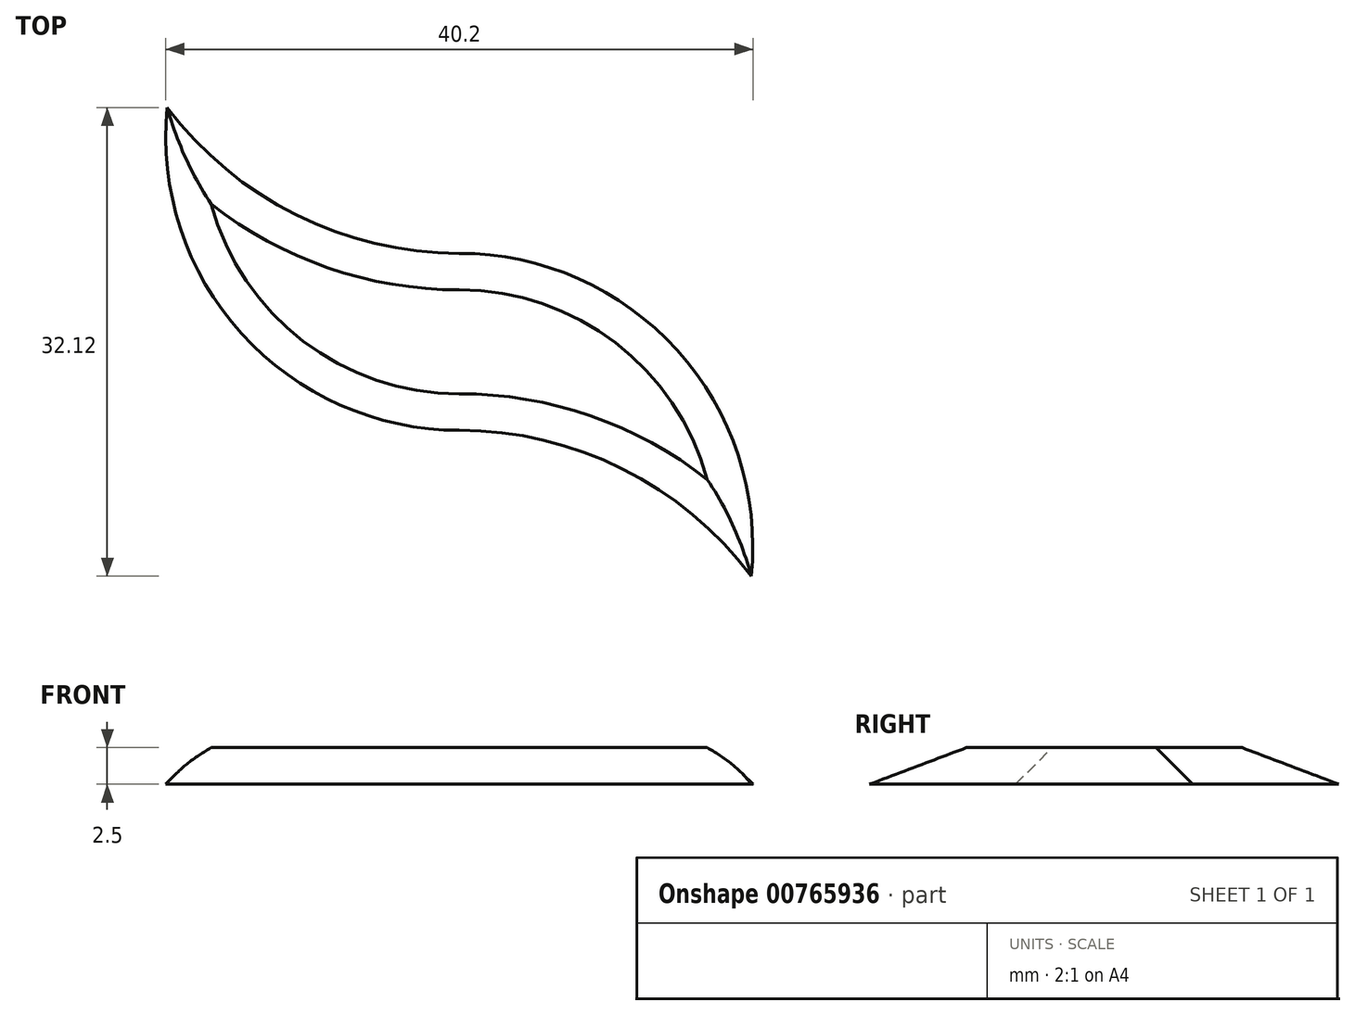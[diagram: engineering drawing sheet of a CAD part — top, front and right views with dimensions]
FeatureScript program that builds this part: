
annotation { "Feature Type Name" : "Feature", "Feature Type Description" : "" }
export const myFeature = defineFeature(function(context is Context, id is Id, definition is map)
    precondition{}
    {
        {
            var Q0;
            Q0=qCreatedBy(makeId("Top.planeOp"),FACE);
            var sketch = newSketch(context, id + "F0", { "sketchPlane" : qUnion([Q0])});
            skLineSegment(sketch, "E0.2", {"start": v(-6.06, -6.06) * mm, "end": v(-6.06, 6.06) * mm});
            skArc(sketch, "E1", {"start": v(-26.06, 16.06) * mm, "mid": v(-20.97, 0.56) * mm, "end": v(-6.06, -6.06) * mm});
            skArc(sketch, "E2", {"start": v(-26.06, 16.06) * mm, "mid": v(-17.24, 8.7) * mm, "end": v(-6.06, 6.06) * mm});
            skPoint(sketch, "E3", {"position": v(13.94, -16.06) * mm});
            skLineSegment(sketch, "E4.bottom", {"start": v(-6.06, -6.06) * mm, "end": v(6.24, -6.06) * mm, "construction": true});
            skLineSegment(sketch, "E4.left", {"start": v(-6.06, -6.06) * mm, "end": v(-6.06, 6.05) * mm, "construction": true});
            skArc(sketch, "E5", {"start": v(13.94, -16.06) * mm, "mid": v(5.12, -8.7) * mm, "end": v(-6.06, -6.06) * mm});
            skLineSegment(sketch, "E6", {"start": v(-6.06, 6.06) * mm, "end": v(10.73, 6.06) * mm, "construction": true});
            skArc(sketch, "E7", {"start": v(13.94, -16.06) * mm, "mid": v(8.85, -0.56) * mm, "end": v(-6.06, 6.06) * mm});
            skSolve(sketch);
        }
        {
            var Q0;
            Q0=makeQuery(id+"F0.imprint","IMPRINT",FACE,{"disambiguationData":[TD([[makeQuery(id+"F0.imprint","IMPRINT",EDGE,{"derivedFrom":sQuery(id+"F0.wireOp",EDGE,"E0.2")}),1.0]])]});
            var Q1;
            Q1=makeQuery(id+"F0.imprint","IMPRINT",FACE,{"disambiguationData":[TD([[makeQuery(id+"F0.imprint","IMPRINT",EDGE,{"derivedFrom":sQuery(id+"F0.wireOp",EDGE,"E0.0")}),1.0]])]});
            extrude(context, id + "F1", {"entities" : qUnion([Q0, Q1]), "depth" : 2.5 * mm, "offsetDistance" : 25 * mm});
        }
        {
            var Q0;
            Q0=makeQuery(id+"F0.imprint","IMPRINT",FACE,{"disambiguationData":[TD([[makeQuery(id+"F0.imprint","IMPRINT",EDGE,{"derivedFrom":sQuery(id+"F0.wireOp",EDGE,"E0.2")}),-1.0]])]});
            extrude(context, id + "F2", {"entities" : qUnion([Q0]), "operationType" : NewBodyOperationType.ADD, "depth" : 2.5 * mm, "offsetDistance" : 25 * mm});
        }
        {
            var Q0;
            Q0=makeQuery(id+"F1.opExtrude","CAP_EDGE",EDGE,{"disambiguationData":[OSD([sQuery(id+"F0.wireOp",EDGE,"E1")])],"isStart":false});
            var Q1;
            Q1=makeQuery(id+"F2.opExtrude","CAP_EDGE",EDGE,{"disambiguationData":[OSD([sQuery(id+"F0.wireOp",EDGE,"E7")])],"isStart":false});
            chamfer(context, id + "F3", {"entities" : qUnion([Q0, Q1]), "width" : 2.5 * mm, "tangentPropagation" : true});
        }
    });
